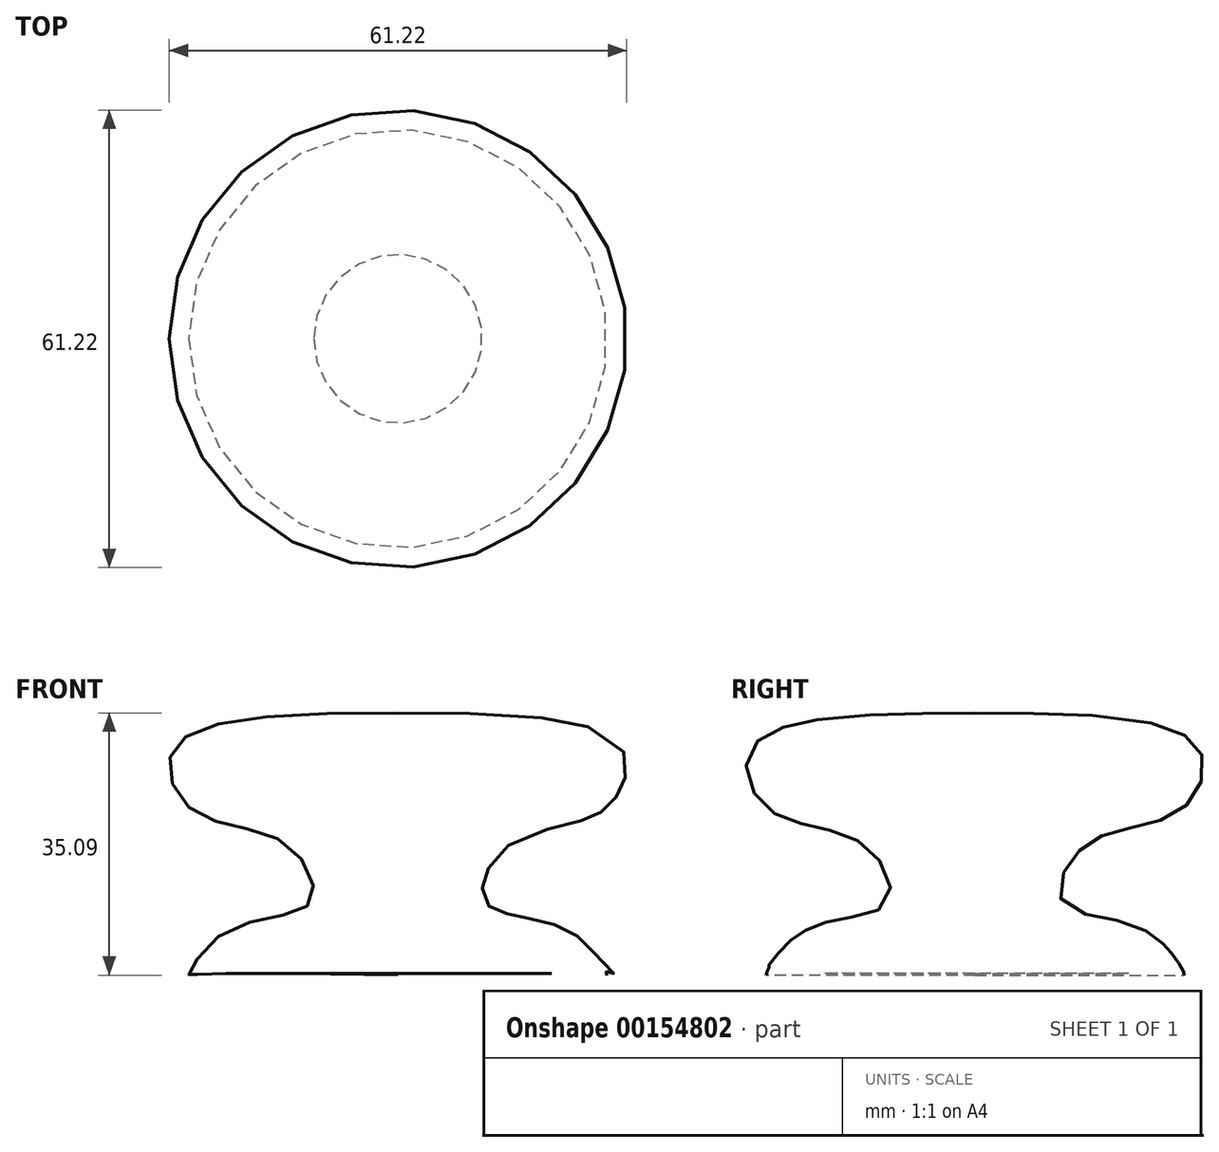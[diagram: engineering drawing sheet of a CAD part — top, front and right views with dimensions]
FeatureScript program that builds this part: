
annotation { "Feature Type Name" : "Feature", "Feature Type Description" : "" }
export const myFeature = defineFeature(function(context is Context, id is Id, definition is map)
    precondition{}
    {
        {
            var Q0;
            Q0=qCreatedBy(makeId("Front.planeOp"),FACE);
            var sketch = newSketch(context, id + "F0", { "sketchPlane" : qUnion([Q0])});
            skLineSegment(sketch, "E0", {"start": v(0, 0) * mm, "end": v(0, 35.05) * mm});
            skFitSpline(sketch, "E1", {"points": [v(0, 0) * mm, v(-27.75, 0) * mm, v(-27.99, 0) * mm, v(-22.96, 5.86) * mm, v(-11.72, 9.69) * mm, v(-15.07, 17.58) * mm, v(-27.27, 21.89) * mm, v(-30.14, 30.02) * mm, v(0, 35.05) * mm], "startDerivative": vector(-217.6, 2.8) * mm, "endDerivative": vector(231.45, 0.16) * mm});
            skSolve(sketch);
        }
        {
            var Q0;
            Q0=makeQuery(id+"F0.imprint","IMPRINT",FACE,{"disambiguationData":[TD([[makeQuery(id+"F0.imprint","IMPRINT",EDGE,{"derivedFrom":sQuery(id+"F0.wireOp",EDGE,"E0")}),1.0]])]});
            var Q1;
            Q1=sQuery(id+"F0.wireOp",EDGE,"E0");
            revolve(context, id + "F1", {"entities" : qUnion([Q0]), "axis" : qUnion([Q1]), "revolveType" : RevolveType.FULL});
        }
    });
